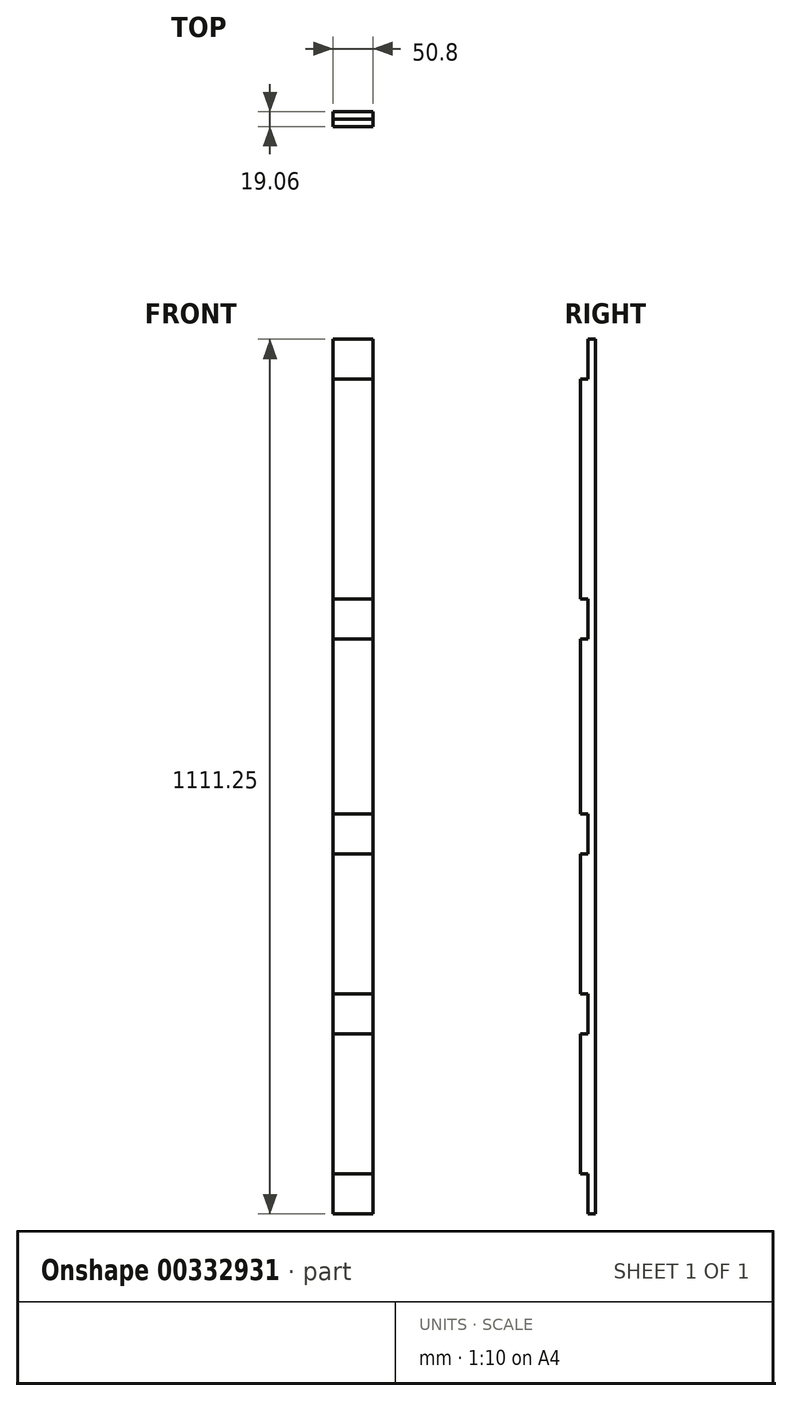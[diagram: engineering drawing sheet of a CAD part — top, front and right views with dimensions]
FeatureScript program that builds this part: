
annotation { "Feature Type Name" : "Feature", "Feature Type Description" : "" }
export const myFeature = defineFeature(function(context is Context, id is Id, definition is map)
    precondition{}
    {
        {
            var Q0;
            Q0=qCreatedBy(makeId("Top.planeOp"),FACE);
            var sketch = newSketch(context, id + "F0", { "sketchPlane" : qUnion([Q0])});
            skLineSegment(sketch, "E0.bottom", {"start": v(25.4, 9.53) * mm, "end": v(-25.4, 9.53) * mm});
            skLineSegment(sketch, "E0.top", {"start": v(25.4, -9.53) * mm, "end": v(-25.4, -9.53) * mm});
            skLineSegment(sketch, "E0.left", {"start": v(25.4, 9.53) * mm, "end": v(25.4, -9.52) * mm});
            skLineSegment(sketch, "E0.right", {"start": v(-25.4, 9.53) * mm, "end": v(-25.4, -9.53) * mm});
            skPoint(sketch, "E0.middle", {"position": v(0, 0) * mm});
            skSolve(sketch);
        }
        {
            var Q0;
            Q0=makeQuery(id+"F0.imprint","IMPRINT",FACE,{"disambiguationData":[TD([[makeQuery(id+"F0.imprint","IMPRINT",EDGE,{"derivedFrom":sQuery(id+"F0.wireOp",EDGE,"E0.bottom")}),1.0]])]});
            extrude(context, id + "F1", {"entities" : qUnion([Q0]), "depth" : 1111.25 * mm});
        }
        {
            var Q0;
            Q0=qCreatedBy(makeId("Front.planeOp"),FACE);
            var sketch = newSketch(context, id + "F2", { "sketchPlane" : qUnion([Q0])});
            skLineSegment(sketch, "E1.bottom", {"start": v(-38.77, 0) * mm, "end": v(83.66, 0) * mm});
            skLineSegment(sketch, "E1.top", {"start": v(-38.77, 50.8) * mm, "end": v(83.66, 50.8) * mm});
            skLineSegment(sketch, "E1.left", {"start": v(-38.77, 0) * mm, "end": v(-38.77, 50.8) * mm});
            skLineSegment(sketch, "E1.right", {"start": v(83.66, 0) * mm, "end": v(83.66, 50.8) * mm});
            skLineSegment(sketch, "E2.bottom", {"start": v(-44.21, 730.25) * mm, "end": v(49.65, 730.25) * mm});
            skLineSegment(sketch, "E2.top", {"start": v(-44.21, 781.05) * mm, "end": v(49.65, 781.05) * mm});
            skLineSegment(sketch, "E2.left", {"start": v(-44.21, 730.25) * mm, "end": v(-44.21, 781.05) * mm});
            skLineSegment(sketch, "E2.right", {"start": v(49.65, 730.25) * mm, "end": v(49.65, 781.05) * mm});
            skLineSegment(sketch, "E3.bottom", {"start": v(-210.36, 1060.45) * mm, "end": v(132.8, 1060.45) * mm});
            skLineSegment(sketch, "E3.top", {"start": v(-210.36, 1111.25) * mm, "end": v(132.8, 1111.25) * mm});
            skLineSegment(sketch, "E3.left", {"start": v(-210.36, 1060.45) * mm, "end": v(-210.36, 1111.25) * mm});
            skLineSegment(sketch, "E3.right", {"start": v(132.8, 1060.45) * mm, "end": v(132.8, 1111.25) * mm});
            skLineSegment(sketch, "E4.bottom", {"start": v(-100.29, 228.6) * mm, "end": v(67.2, 228.6) * mm});
            skLineSegment(sketch, "E4.top", {"start": v(-100.29, 279.4) * mm, "end": v(67.2, 279.4) * mm});
            skLineSegment(sketch, "E4.left", {"start": v(-100.29, 228.6) * mm, "end": v(-100.29, 279.4) * mm});
            skLineSegment(sketch, "E4.right", {"start": v(67.2, 228.6) * mm, "end": v(67.2, 279.4) * mm});
            skLineSegment(sketch, "E5.bottom", {"start": v(-120.97, 508) * mm, "end": v(63.07, 508) * mm});
            skLineSegment(sketch, "E5.top", {"start": v(-120.97, 457.2) * mm, "end": v(63.07, 457.2) * mm});
            skLineSegment(sketch, "E5.left", {"start": v(-120.97, 508) * mm, "end": v(-120.97, 457.2) * mm});
            skLineSegment(sketch, "E5.right", {"start": v(63.07, 508) * mm, "end": v(63.07, 457.2) * mm});
            skSolve(sketch);
        }
        {
            var Q0;
            Q0=qSketchRegion(id+"F2",true);
            extrude(context, id + "F3", {"entities" : qUnion([Q0]), "operationType" : NewBodyOperationType.REMOVE, "depth" : 25.4 * mm});
        }
    });
